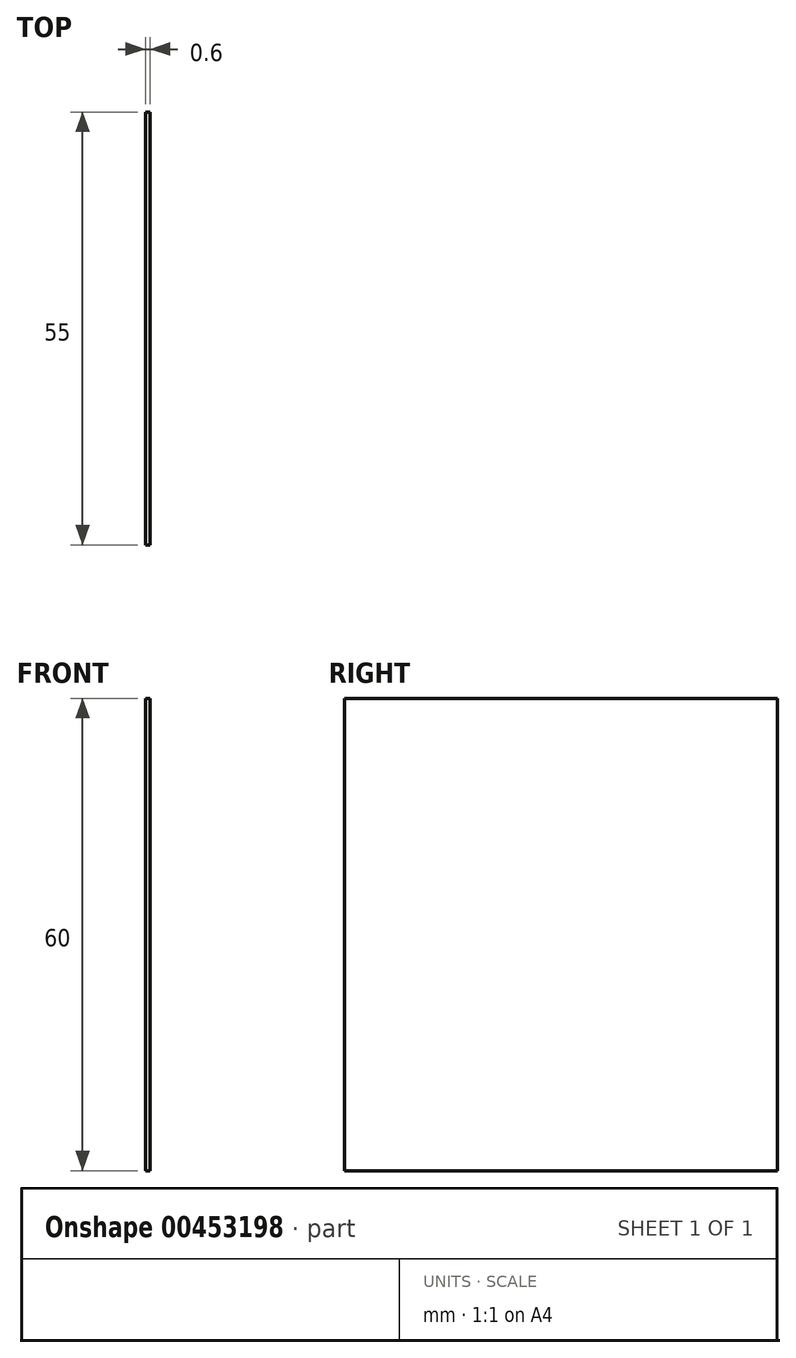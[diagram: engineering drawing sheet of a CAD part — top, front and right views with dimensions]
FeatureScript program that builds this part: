
annotation { "Feature Type Name" : "Feature", "Feature Type Description" : "" }
export const myFeature = defineFeature(function(context is Context, id is Id, definition is map)
    precondition{}
    {
        {
            var Q0;
            Q0=qCreatedBy(makeId("Right.planeOp"),FACE);
            var sketch = newSketch(context, id + "F0", { "sketchPlane" : qUnion([Q0])});
            skLineSegment(sketch, "E0.bottom", {"start": v(-22.77, 33.1) * mm, "end": v(32.23, 33.1) * mm});
            skLineSegment(sketch, "E0.top", {"start": v(-22.77, -26.9) * mm, "end": v(32.23, -26.9) * mm});
            skLineSegment(sketch, "E0.left", {"start": v(-22.77, 33.1) * mm, "end": v(-22.77, -26.9) * mm});
            skLineSegment(sketch, "E0.right", {"start": v(32.23, 33.1) * mm, "end": v(32.23, -26.9) * mm});
            skSolve(sketch);
        }
        {
            var Q0;
            Q0=makeQuery(id+"F0.imprint","IMPRINT",FACE,{"disambiguationData":[TD([[makeQuery(id+"F0.imprint","IMPRINT",EDGE,{"derivedFrom":sQuery(id+"F0.wireOp",EDGE,"E0.bottom")}),-1.0]])]});
            extrude(context, id + "F1", {"entities" : qUnion([Q0]), "depth" : 0.6 * mm});
        }
    });
